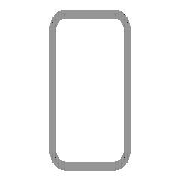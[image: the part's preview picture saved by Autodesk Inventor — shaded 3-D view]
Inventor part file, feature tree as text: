
AUTODESK INVENTOR PART (.ipt)
format: ipt  version: 2025.3 (Build 293356000, 356)  size: 133,120 bytes
history: native  units: mm (DEFAULTED — no unit token found)
features: other x4, sketch x1, plane x1
ambient origin geometry x8: Origin, YZ Plane, XZ Plane, XY Plane, X Axis, Y Axis, Z Axis, Center Point
bodies: Solid1 (feature_tree), Body (feature_tree)
feature tree (6):
  parser-record x1  (decoder bookkeeping rows leaked as tree rows — omitted from the tree; the rows remain in map.json)
  other  "Driven Length"
  other  "Start Plane"
  other  "End Plane"
  sketch  "Sketch3"  dims[d3=585.0mm d4=0.0mm d7=6.0mm d9=40.0mm d11=80.0mm d12=3.0mm d13=20.0mm d14=605.0mm d15=20.0mm d16=40.0mm d17=90.0deg d18=585.0mm]
  plane  "Work Plane3"
